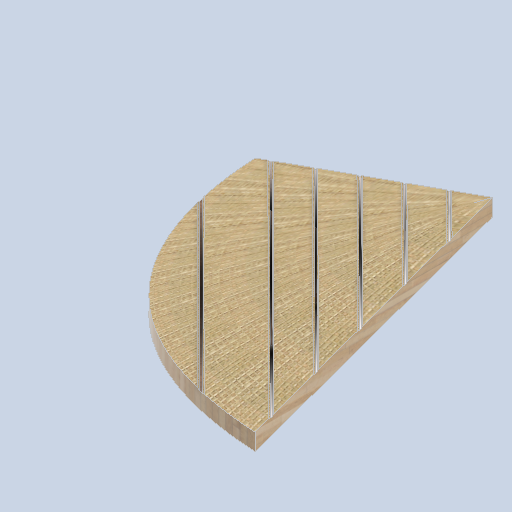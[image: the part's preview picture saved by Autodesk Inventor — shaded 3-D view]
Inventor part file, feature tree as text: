
AUTODESK INVENTOR PART (.ipt)
format: ipt  version: 2024.2 (Build 282272000, 272)  size: 1,026,560 bytes
history: native  units: mm
features: sketch x19, loft x7, plane x6, extrude x3, fillet x1
ambient origin geometry x8: Origin, YZ Plane, XZ Plane, XY Plane, X Axis, Y Axis, Z Axis, Center Point
bodies: Solid1 (feature_tree)
feature tree (36):
  sketch  "Sketch1"  dims[d6=2000.0mm d7=0.0mm d8=90.0deg d9=90.0deg d11=12.287118mm]
  plane  "Work Plane1"
  plane  "Work Plane2"
  plane  "Work Plane3"
  sketch  "Sketch2"  dims[d12=150.0mm d13=19.128809mm]
  plane  "Work Plane4"
  sketch  "Sketch3"  dims[d14=150.0mm d15=150.0mm]
  plane  "Work Plane5"
  loft  "Loft1"
  loft  "Loft2"
  loft  "Loft3"
  loft  "Loft4"
  loft  "Loft5"
  loft  "Loft6"
  plane  "Work Plane6"
  extrude  "Extrusion1"  TaperAngle=0.0deg  [1 undecoded]
  fillet  "Fillet1"  Radius=400.0mm
  sketch  "Sketch17"  dims[d46=20.0mm]
  extrude  "Extrusion3"  Depth=20.0mm
  extrude  "Extrusion4"  Depth=10.0mm
  loft  "Loft7"
  sketch  "Sketch4"  dims[d16=0.0mm d17=90.0deg d18=0.0mm d19=90.0deg]
  sketch  "Sketch5"  dims[d20=0.0mm d21=90.0deg d23=20.0mm]
  sketch  "Sketch6"  dims[d24=400.0mm d26=20.0mm]
  sketch  "Sketch7"  dims[d27=0.0mm d28=90.0deg d29=0.0mm d30=90.0deg d31=400.0mm]
  sketch  "Sketch8"  dims[d32=10.0mm d33=20.0mm]
  sketch  "Sketch9"  dims[d34=400.0mm d35=10.0mm]
  sketch  "Sketch10"  dims[d36=20.0mm d37=0.0mm d38=90.0deg]
  sketch  "Sketch11"  dims[d39=0.0mm d40=90.0deg]
  sketch  "Sketch12"  dims[d41=400.0mm]
  sketch  "Sketch13"  dims[d42=10.0mm]
  sketch  "Sketch14"  dims[d43=20.0mm]
  sketch  "Sketch15"  dims[d44=400.0mm]
  sketch  "Sketch16"  dims[d45=10.0mm]
  sketch  "Sketch18"  dims[d47=0.0mm d48=90.0deg]
  sketch  "Sketch19"  dims[d49=0.0mm d50=90.0deg d51=400.0mm d52=10.0mm d53=20.0mm d54=400.0mm d55=10.0mm d56=20.0mm d57=0.0mm d58=90.0deg d59=0.0mm d60=90.0deg d61=400.0mm d62=10.0mm d63=20.0mm d64=400.0mm d66=20.0mm d67=0.0mm d68=90.0deg d69=0.0mm d70=90.0deg d71=45.0deg d73=20.0mm d74=0.0mm d75=0.0mm d76=10.0mm d79=280.0mm d80=0.0mm d81=380.0mm d82=0.0mm d83=0.0mm d84=90.0deg d85=0.0mm d86=90.0deg]
note: 1 required parameter value undecoded (feature->parameter linkage not recoverable at this tier; creation-order binding heuristic only, values carry confidence <= 0.55)
